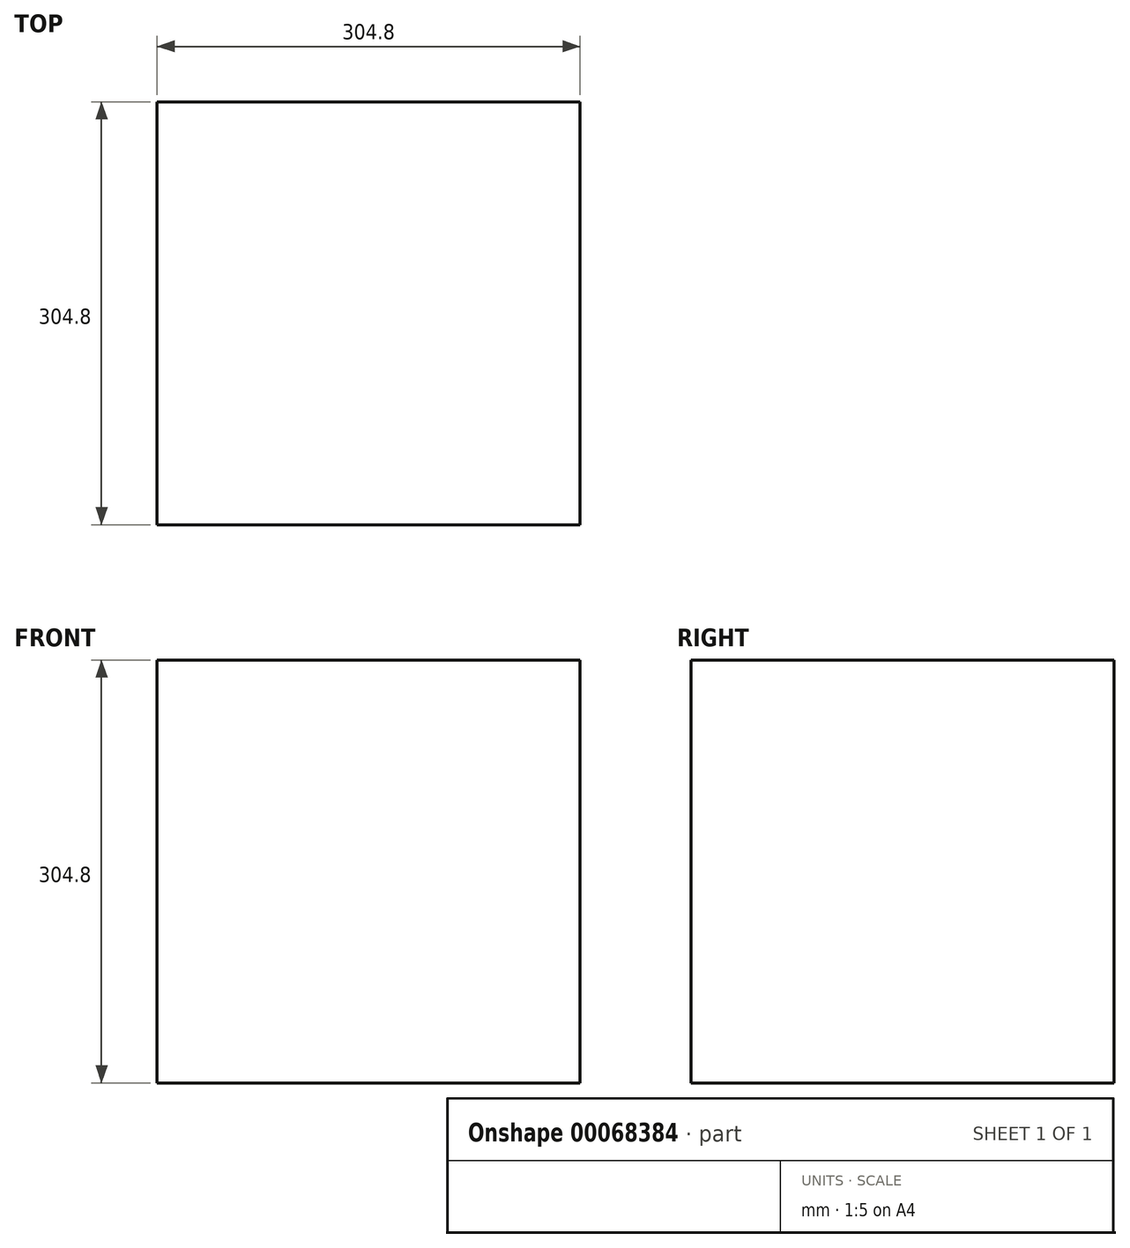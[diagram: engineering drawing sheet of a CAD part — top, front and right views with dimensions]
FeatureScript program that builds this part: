
annotation { "Feature Type Name" : "Feature", "Feature Type Description" : "" }
export const myFeature = defineFeature(function(context is Context, id is Id, definition is map)
    precondition{}
    {
        {
            var Q0;
            Q0=qCreatedBy(makeId("Front.planeOp"),FACE);
            var sketch = newSketch(context, id + "F0", { "sketchPlane" : qUnion([Q0])});
            skLineSegment(sketch, "E0.rect.bottom", {"start": v(152.4, 152.4) * mm, "end": v(-152.4, 152.4) * mm});
            skLineSegment(sketch, "E0.rect.top", {"start": v(152.4, -152.4) * mm, "end": v(-152.4, -152.4) * mm});
            skLineSegment(sketch, "E0.rect.left", {"start": v(152.4, 152.4) * mm, "end": v(152.4, -152.4) * mm});
            skLineSegment(sketch, "E0.rect.right", {"start": v(-152.4, 152.4) * mm, "end": v(-152.4, -152.4) * mm});
            skPoint(sketch, "E0.rect.middle", {"position": v(0, 0) * mm});
            skSolve(sketch);
        }
        {
            var Q0;
            Q0=makeQuery(id+"F0.imprint","IMPRINT",FACE,{"disambiguationData":[TD([[makeQuery(id+"F0.imprint","IMPRINT",EDGE,{"derivedFrom":sQuery(id+"F0.wireOp",EDGE,"E0.rect.bottom")}),1.0]])]});
            extrude(context, id + "F1", {"entities" : qUnion([Q0]), "depth" : 304.8 * mm});
        }
    });
